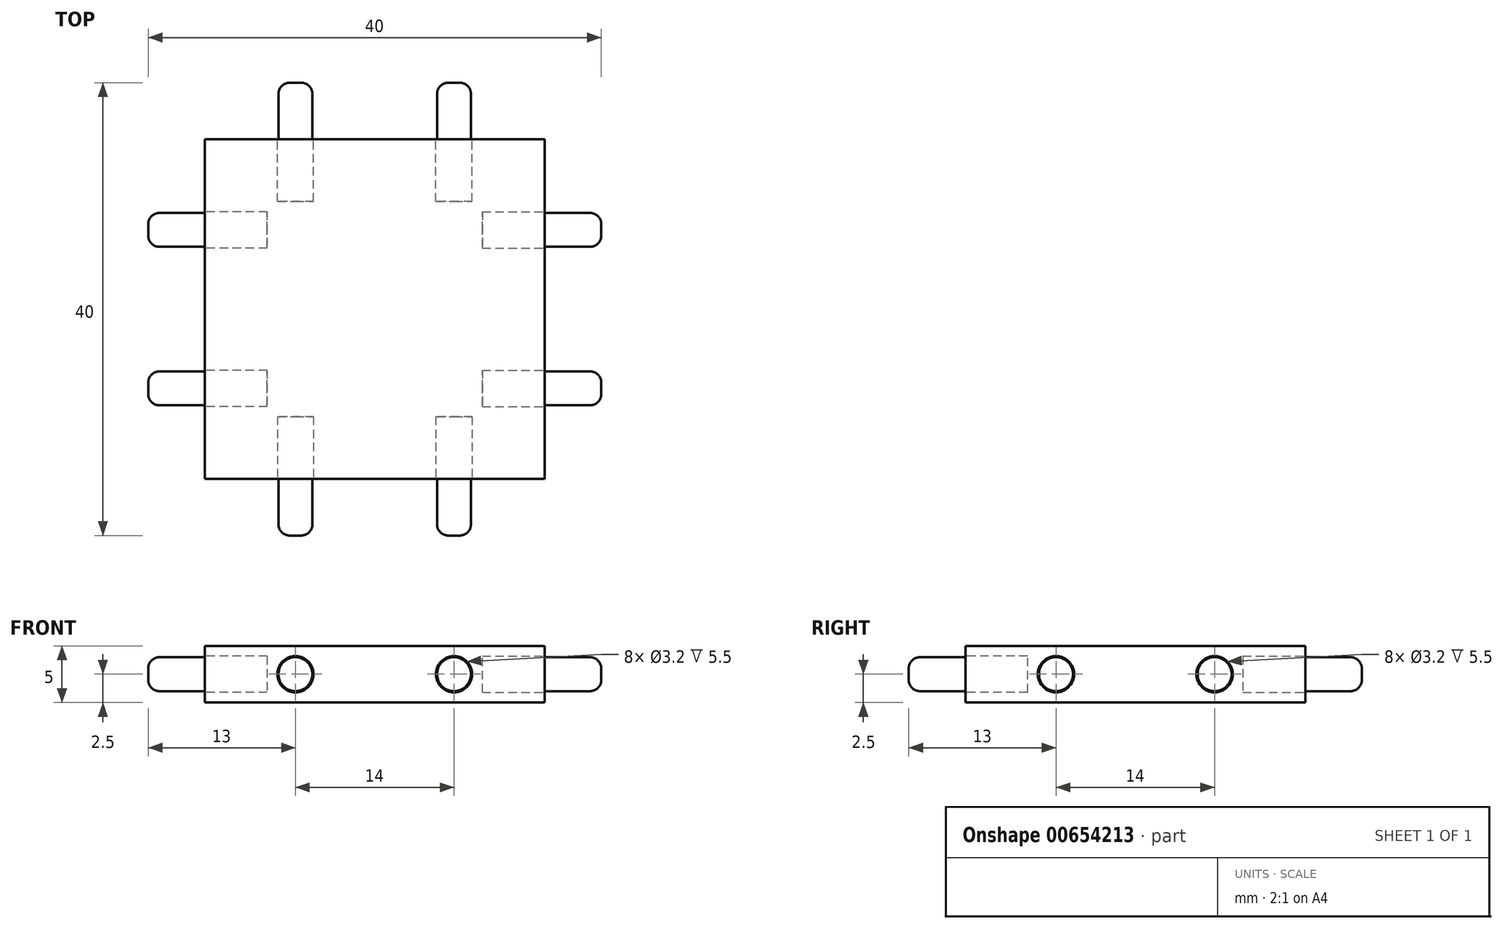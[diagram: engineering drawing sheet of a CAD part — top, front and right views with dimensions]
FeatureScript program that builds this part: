
annotation { "Feature Type Name" : "Feature", "Feature Type Description" : "" }
export const myFeature = defineFeature(function(context is Context, id is Id, definition is map)
    precondition{}
    {
        {
            var Q0;
            Q0=qCreatedBy(makeId("Top.planeOp"),FACE);
            var sketch = newSketch(context, id + "F0", { "sketchPlane" : qUnion([Q0])});
            skLineSegment(sketch, "E0.bottom", {"start": v(15, 15) * mm, "end": v(-15, 15) * mm});
            skLineSegment(sketch, "E0.top", {"start": v(15, -15) * mm, "end": v(-15, -15) * mm});
            skLineSegment(sketch, "E0.left", {"start": v(15, 15) * mm, "end": v(15, -15) * mm});
            skLineSegment(sketch, "E0.right", {"start": v(-15, 15) * mm, "end": v(-15, -15) * mm});
            skPoint(sketch, "E0.middle", {"position": v(0, 0) * mm});
            skSolve(sketch);
        }
        {
            var Q0;
            Q0 = qSketchRegion(id + "F0", true);
            extrude(context, id + "F1", {"entities" : qUnion([Q0]), "depth" : 5 * mm, "offsetDistance" : 25 * mm});
        }
        {
            var Q0;
            Q0=makeQuery(id+"F1.opExtrude","SWEPT_FACE",FACE,{"disambiguationData":[OSD([sQuery(id+"F0.wireOp",EDGE,"E0.top")])]});
            var sketch = newSketch(context, id + "F2", { "sketchPlane" : qUnion([Q0])});
            skLineSegment(sketch, "E1", {"start": v(-15, 2.5) * mm, "end": v(15, 2.5) * mm, "construction": true});
            skPoint(sketch, "E2", {"position": v(-7, 2.5) * mm});
            skPoint(sketch, "E3", {"position": v(7, 2.5) * mm});
            skPoint(sketch, "E4", {"position": v(15, 2.5) * mm});
            skCircle(sketch, "E5", {"center": v(-7, 2.5) * mm, "radius": 1.5 * mm});
            skCircle(sketch, "E6", {"center": v(7, 2.5) * mm, "radius": 1.5 * mm});
            skSolve(sketch);
        }
        {
            var Q0;
            Q0=makeQuery(id+"F1.opExtrude","SWEPT_FACE",FACE,{"disambiguationData":[OSD([sQuery(id+"F0.wireOp",EDGE,"E0.right")])]});
            var sketch = newSketch(context, id + "F3", { "sketchPlane" : qUnion([Q0])});
            skLineSegment(sketch, "E7", {"start": v(-15, 2.5) * mm, "end": v(15, 2.5) * mm, "construction": true});
            skPoint(sketch, "E8", {"position": v(7, 2.5) * mm});
            skPoint(sketch, "E9", {"position": v(-7, 2.5) * mm});
            skCircle(sketch, "E10", {"center": v(-7, 2.5) * mm, "radius": 1.5 * mm});
            skCircle(sketch, "E11", {"center": v(7, 2.5) * mm, "radius": 1.5 * mm});
            skSolve(sketch);
        }
        {
            var Q0;
            Q0=makeQuery(id+"F1.opExtrude","SWEPT_FACE",FACE,{"disambiguationData":[OSD([sQuery(id+"F0.wireOp",EDGE,"E0.bottom")])]});
            var sketch = newSketch(context, id + "F4", { "sketchPlane" : qUnion([Q0])});
            skLineSegment(sketch, "E12", {"start": v(-15, 2.5) * mm, "end": v(15, 2.5) * mm, "construction": true});
            skPoint(sketch, "E13", {"position": v(-7, 2.5) * mm});
            skPoint(sketch, "E14", {"position": v(7, 2.5) * mm});
            skCircle(sketch, "E15", {"center": v(-7, 2.5) * mm, "radius": 1.5 * mm});
            skCircle(sketch, "E16", {"center": v(7, 2.5) * mm, "radius": 1.5 * mm});
            skSolve(sketch);
        }
        {
            var Q0;
            Q0=makeQuery(id+"F1.opExtrude","SWEPT_FACE",FACE,{"disambiguationData":[OSD([sQuery(id+"F0.wireOp",EDGE,"E0.left")])]});
            var sketch = newSketch(context, id + "F5", { "sketchPlane" : qUnion([Q0])});
            skLineSegment(sketch, "E17", {"start": v(-15, 2.5) * mm, "end": v(15, 2.5) * mm, "construction": true});
            skPoint(sketch, "E18", {"position": v(-7, 2.5) * mm});
            skPoint(sketch, "E19", {"position": v(7, 2.5) * mm});
            skCircle(sketch, "E20", {"center": v(-7, 2.5) * mm, "radius": 1.5 * mm});
            skCircle(sketch, "E21", {"center": v(7, 2.5) * mm, "radius": 1.5 * mm});
            skSolve(sketch);
        }
        {
            var Q0;
            Q0=makeQuery(id+"F5.imprint","IMPRINT",FACE,{"disambiguationData":[TD([[makeQuery(id+"F5.imprint","IMPRINT",EDGE,{"derivedFrom":sQuery(id+"F5.wireOp",EDGE,"E20")}),1.0]])]});
            var Q1;
            Q1=makeQuery(id+"F5.imprint","IMPRINT",FACE,{"disambiguationData":[TD([[makeQuery(id+"F5.imprint","IMPRINT",EDGE,{"derivedFrom":sQuery(id+"F5.wireOp",EDGE,"E21")}),1.0]])]});
            extrude(context, id + "F6", {"entities" : qUnion([Q0, Q1]), "operationType" : NewBodyOperationType.ADD, "depth" : 5 * mm, "offsetDistance" : 25 * mm});
        }
        {
            var Q0;
            Q0=makeQuery(id+"F4.imprint","IMPRINT",FACE,{"disambiguationData":[TD([[makeQuery(id+"F4.imprint","IMPRINT",EDGE,{"derivedFrom":sQuery(id+"F4.wireOp",EDGE,"E15")}),1.0]])]});
            var Q1;
            Q1=makeQuery(id+"F4.imprint","IMPRINT",FACE,{"disambiguationData":[TD([[makeQuery(id+"F4.imprint","IMPRINT",EDGE,{"derivedFrom":sQuery(id+"F4.wireOp",EDGE,"E16")}),1.0]])]});
            extrude(context, id + "F7", {"entities" : qUnion([Q0, Q1]), "operationType" : NewBodyOperationType.ADD, "depth" : 5 * mm, "offsetDistance" : 25 * mm});
        }
        {
            var Q0;
            Q0=makeQuery(id+"F3.imprint","IMPRINT",FACE,{"disambiguationData":[TD([[makeQuery(id+"F3.imprint","IMPRINT",EDGE,{"derivedFrom":sQuery(id+"F3.wireOp",EDGE,"E10")}),1.0]])]});
            var Q1;
            Q1=makeQuery(id+"F3.imprint","IMPRINT",FACE,{"disambiguationData":[TD([[makeQuery(id+"F3.imprint","IMPRINT",EDGE,{"derivedFrom":sQuery(id+"F3.wireOp",EDGE,"E11")}),1.0]])]});
            extrude(context, id + "F8", {"entities" : qUnion([Q0, Q1]), "operationType" : NewBodyOperationType.ADD, "depth" : 5 * mm, "offsetDistance" : 25 * mm});
        }
        {
            var Q0;
            Q0=makeQuery(id+"F2.imprint","IMPRINT",FACE,{"disambiguationData":[TD([[makeQuery(id+"F2.imprint","IMPRINT",EDGE,{"derivedFrom":sQuery(id+"F2.wireOp",EDGE,"E6")}),1.0]])]});
            var Q1;
            Q1=makeQuery(id+"F2.imprint","IMPRINT",FACE,{"disambiguationData":[TD([[makeQuery(id+"F2.imprint","IMPRINT",EDGE,{"derivedFrom":sQuery(id+"F2.wireOp",EDGE,"E5")}),1.0]])]});
            extrude(context, id + "F9", {"entities" : qUnion([Q0, Q1]), "operationType" : NewBodyOperationType.ADD, "depth" : 5 * mm, "offsetDistance" : 25 * mm});
        }
        {
            var Q0;
            Q0=makeQuery(id+"F6.opExtrude","CAP_FACE",FACE,{"disambiguationData":[OSD([sQuery(id+"F5.wireOp",EDGE,"E20")])],"isStart":false});
            var Q1;
            Q1=makeQuery(id+"F6.opExtrude","CAP_EDGE",EDGE,{"disambiguationData":[OSD([sQuery(id+"F5.wireOp",EDGE,"E21")])],"isStart":false});
            var Q2;
            Q2=makeQuery(id+"F7.opExtrude","CAP_EDGE",EDGE,{"disambiguationData":[OSD([sQuery(id+"F4.wireOp",EDGE,"E15")])],"isStart":false});
            var Q3;
            Q3=makeQuery(id+"F7.opExtrude","CAP_EDGE",EDGE,{"disambiguationData":[OSD([sQuery(id+"F4.wireOp",EDGE,"E16")])],"isStart":false});
            var Q4;
            Q4=makeQuery(id+"F8.opExtrude","CAP_EDGE",EDGE,{"disambiguationData":[OSD([sQuery(id+"F3.wireOp",EDGE,"E10")])],"isStart":false});
            var Q5;
            Q5=makeQuery(id+"F8.opExtrude","CAP_EDGE",EDGE,{"disambiguationData":[OSD([sQuery(id+"F3.wireOp",EDGE,"E11")])],"isStart":false});
            var Q6;
            Q6=makeQuery(id+"F9.opExtrude","CAP_EDGE",EDGE,{"disambiguationData":[OSD([sQuery(id+"F2.wireOp",EDGE,"E6")])],"isStart":false});
            var Q7;
            Q7=makeQuery(id+"F9.opExtrude","CAP_EDGE",EDGE,{"disambiguationData":[OSD([sQuery(id+"F2.wireOp",EDGE,"E5")])],"isStart":false});
            fillet(context, id + "F10", {"entities" : qUnion([Q0, Q1, Q2, Q3, Q4, Q5, Q6, Q7]), "radius" : 1 * mm, "tangentPropagation" : true, "allowEdgeOverflow" : false});
        }
        {
            var Q0;
            Q0=qCreatedBy(makeId("Top.planeOp"),FACE);
            var sketch = newSketch(context, id + "F11", { "sketchPlane" : qUnion([Q0])});
            skLineSegment(sketch, "E22.bottom", {"start": v(15, 15) * mm, "end": v(-15, 15) * mm});
            skLineSegment(sketch, "E22.top", {"start": v(15, -15) * mm, "end": v(-15, -15) * mm});
            skLineSegment(sketch, "E22.left", {"start": v(15, 15) * mm, "end": v(15, -15) * mm});
            skLineSegment(sketch, "E22.right", {"start": v(-15, 15) * mm, "end": v(-15, -15) * mm});
            skPoint(sketch, "E22.middle", {"position": v(0, 0) * mm});
            skSolve(sketch);
        }
        {
            var Q0;
            Q0=makeQuery(id+"F11.imprint","IMPRINT",FACE,{"disambiguationData":[TD([[makeQuery(id+"F11.imprint","IMPRINT",EDGE,{"derivedFrom":sQuery(id+"F11.wireOp",EDGE,"E22.bottom")}),1.0]])]});
            extrude(context, id + "F12", {"entities" : qUnion([Q0]), "depth" : 5 * mm, "offsetDistance" : 25 * mm});
        }
        {
            var Q0;
            Q0=makeQuery(id+"F12.opExtrude","SWEPT_FACE",FACE,{"disambiguationData":[OSD([sQuery(id+"F11.wireOp",EDGE,"E22.top")])]});
            var sketch = newSketch(context, id + "F13", { "sketchPlane" : qUnion([Q0])});
            skLineSegment(sketch, "E23", {"start": v(-15, 2.5) * mm, "end": v(15, 2.5) * mm, "construction": true});
            skPoint(sketch, "E24", {"position": v(-7, 2.5) * mm});
            skPoint(sketch, "E25", {"position": v(7, 2.5) * mm});
            skCircle(sketch, "E26", {"center": v(-7, 2.5) * mm, "radius": 1.6 * mm});
            skCircle(sketch, "E27", {"center": v(7, 2.5) * mm, "radius": 1.6 * mm});
            skSolve(sketch);
        }
        {
            var Q0;
            Q0=makeQuery(id+"F13.imprint","IMPRINT",FACE,{"disambiguationData":[TD([[makeQuery(id+"F13.imprint","IMPRINT",EDGE,{"derivedFrom":sQuery(id+"F13.wireOp",EDGE,"E26")}),1.0]])]});
            var Q1;
            Q1=makeQuery(id+"F13.imprint","IMPRINT",FACE,{"disambiguationData":[TD([[makeQuery(id+"F13.imprint","IMPRINT",EDGE,{"derivedFrom":sQuery(id+"F13.wireOp",EDGE,"E27")}),1.0]])]});
            extrude(context, id + "F14", {"entities" : qUnion([Q0, Q1]), "operationType" : NewBodyOperationType.REMOVE, "oppositeDirection" : true, "depth" : 5.5 * mm, "offsetDistance" : 25 * mm});
        }
        {
            var Q0;
            Q0=makeQuery(id+"F12.opExtrude","SWEPT_FACE",FACE,{"disambiguationData":[OSD([sQuery(id+"F11.wireOp",EDGE,"E22.left")])]});
            var sketch = newSketch(context, id + "F15", { "sketchPlane" : qUnion([Q0])});
            skLineSegment(sketch, "E28", {"start": v(-15, 2.5) * mm, "end": v(15, 2.5) * mm, "construction": true});
            skPoint(sketch, "E29", {"position": v(-7, 2.5) * mm});
            skPoint(sketch, "E30", {"position": v(7, 2.5) * mm});
            skCircle(sketch, "E31", {"center": v(-7, 2.5) * mm, "radius": 1.6 * mm});
            skCircle(sketch, "E32", {"center": v(7, 2.5) * mm, "radius": 1.6 * mm});
            skSolve(sketch);
        }
        {
            var Q0;
            Q0=makeQuery(id+"F15.imprint","IMPRINT",FACE,{"disambiguationData":[TD([[makeQuery(id+"F15.imprint","IMPRINT",EDGE,{"derivedFrom":sQuery(id+"F15.wireOp",EDGE,"E31")}),1.0]])]});
            var Q1;
            Q1=makeQuery(id+"F15.imprint","IMPRINT",FACE,{"disambiguationData":[TD([[makeQuery(id+"F15.imprint","IMPRINT",EDGE,{"derivedFrom":sQuery(id+"F15.wireOp",EDGE,"E32")}),1.0]])]});
            extrude(context, id + "F16", {"entities" : qUnion([Q0, Q1]), "operationType" : NewBodyOperationType.REMOVE, "oppositeDirection" : true, "depth" : 5.5 * mm, "offsetDistance" : 25 * mm});
        }
        {
            var Q0;
            Q0=makeQuery(id+"F12.opExtrude","SWEPT_FACE",FACE,{"disambiguationData":[OSD([sQuery(id+"F11.wireOp",EDGE,"E22.bottom")])]});
            var sketch = newSketch(context, id + "F17", { "sketchPlane" : qUnion([Q0])});
            skLineSegment(sketch, "E33", {"start": v(-15, 2.5) * mm, "end": v(15, 2.5) * mm, "construction": true});
            skPoint(sketch, "E34", {"position": v(-7, 2.5) * mm});
            skPoint(sketch, "E35", {"position": v(7, 2.5) * mm});
            skCircle(sketch, "E36", {"center": v(-7, 2.5) * mm, "radius": 1.6 * mm});
            skCircle(sketch, "E37", {"center": v(7, 2.5) * mm, "radius": 1.6 * mm});
            skSolve(sketch);
        }
        {
            var Q0;
            Q0=makeQuery(id+"F17.imprint","IMPRINT",FACE,{"disambiguationData":[TD([[makeQuery(id+"F17.imprint","IMPRINT",EDGE,{"derivedFrom":sQuery(id+"F17.wireOp",EDGE,"E36")}),1.0]])]});
            var Q1;
            Q1=makeQuery(id+"F17.imprint","IMPRINT",FACE,{"disambiguationData":[TD([[makeQuery(id+"F17.imprint","IMPRINT",EDGE,{"derivedFrom":sQuery(id+"F17.wireOp",EDGE,"E37")}),1.0]])]});
            extrude(context, id + "F18", {"entities" : qUnion([Q0, Q1]), "operationType" : NewBodyOperationType.REMOVE, "oppositeDirection" : true, "depth" : 5.5 * mm, "offsetDistance" : 25 * mm});
        }
        {
            var Q0;
            Q0=makeQuery(id+"F12.opExtrude","SWEPT_FACE",FACE,{"disambiguationData":[OSD([sQuery(id+"F11.wireOp",EDGE,"E22.right")])]});
            var sketch = newSketch(context, id + "F19", { "sketchPlane" : qUnion([Q0])});
            skLineSegment(sketch, "E38", {"start": v(-15, 2.5) * mm, "end": v(15, 2.5) * mm, "construction": true});
            skPoint(sketch, "E39", {"position": v(-7, 2.5) * mm});
            skPoint(sketch, "E40", {"position": v(7, 2.5) * mm});
            skCircle(sketch, "E41", {"center": v(-7, 2.5) * mm, "radius": 1.6 * mm});
            skCircle(sketch, "E42", {"center": v(7, 2.5) * mm, "radius": 1.6 * mm});
            skSolve(sketch);
        }
        {
            var Q0;
            Q0=makeQuery(id+"F19.imprint","IMPRINT",FACE,{"disambiguationData":[TD([[makeQuery(id+"F19.imprint","IMPRINT",EDGE,{"derivedFrom":sQuery(id+"F19.wireOp",EDGE,"E41")}),1.0]])]});
            var Q1;
            Q1=makeQuery(id+"F19.imprint","IMPRINT",FACE,{"disambiguationData":[TD([[makeQuery(id+"F19.imprint","IMPRINT",EDGE,{"derivedFrom":sQuery(id+"F19.wireOp",EDGE,"E42")}),1.0]])]});
            extrude(context, id + "F20", {"entities" : qUnion([Q0, Q1]), "operationType" : NewBodyOperationType.REMOVE, "oppositeDirection" : true, "depth" : 5.5 * mm, "offsetDistance" : 25 * mm});
        }
    });
